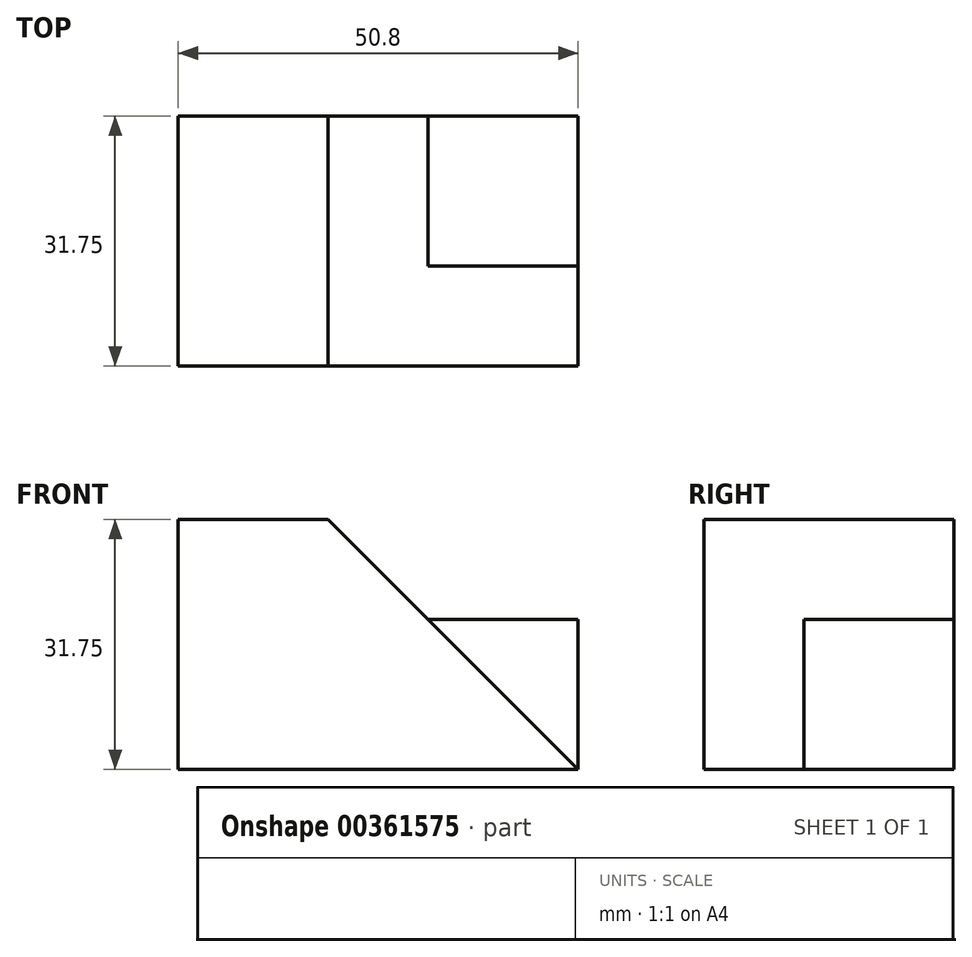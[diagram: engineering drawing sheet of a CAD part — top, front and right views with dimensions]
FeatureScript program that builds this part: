
annotation { "Feature Type Name" : "Feature", "Feature Type Description" : "" }
export const myFeature = defineFeature(function(context is Context, id is Id, definition is map)
    precondition{}
    {
        {
            var Q0;
            Q0=qCreatedBy(makeId("Front.planeOp"),FACE);
            var sketch = newSketch(context, id + "F0", { "sketchPlane" : qUnion([Q0])});
            skLineSegment(sketch, "E0", {"start": v(0, 0) * mm, "end": v(50.8, 0) * mm});
            skLineSegment(sketch, "E1", {"start": v(50.8, 0) * mm, "end": v(50.8, 31.75) * mm});
            skLineSegment(sketch, "E2", {"start": v(50.8, 31.75) * mm, "end": v(0, 31.75) * mm});
            skLineSegment(sketch, "E3", {"start": v(0, 31.75) * mm, "end": v(0, 0) * mm});
            skSolve(sketch);
        }
        {
            var Q0;
            Q0=makeQuery(id+"F0.imprint","IMPRINT",FACE,{"disambiguationData":[TD([[makeQuery(id+"F0.imprint","IMPRINT",EDGE,{"derivedFrom":sQuery(id+"F0.wireOp",EDGE,"E0")}),1.0]])]});
            extrude(context, id + "F1", {"entities" : qUnion([Q0]), "depth" : 31.75 * mm});
        }
        {
            var Q0;
            Q0=makeQuery(id+"F1.opExtrude","CAP_FACE",FACE,{"disambiguationData":[OSD([sQuery(id+"F0.wireOp",EDGE,"E0"),sQuery(id+"F0.wireOp",EDGE,"E1"),sQuery(id+"F0.wireOp",EDGE,"E2"),sQuery(id+"F0.wireOp",EDGE,"E3")])],"isStart":false});
            var sketch = newSketch(context, id + "F2", { "sketchPlane" : qUnion([Q0])});
            skLineSegment(sketch, "E4", {"start": v(19.05, 31.75) * mm, "end": v(31.75, 19.05) * mm});
            skLineSegment(sketch, "E5", {"start": v(31.75, 19.05) * mm, "end": v(50.8, 19.05) * mm});
            skSolve(sketch);
        }
        {
            var Q0;
            {var subQ0=sQuery(id+"F2.wireOp",EDGE,"E4");Q0=makeQuery(id+"F2.imprint","IMPRINT",FACE,{"disambiguationData":[TD([[makeQuery(id+"F2.imprint","IMPRINT",EDGE,{"derivedFrom":subQ0}),1.0]])]});}
            extrude(context, id + "F3", {"entities" : qUnion([Q0]), "operationType" : NewBodyOperationType.REMOVE, "oppositeDirection" : true, "depth" : 31.75 * mm});
        }
        {
            var Q0;
            Q0=makeQuery(id+"F1.opExtrude","CAP_FACE",FACE,{"disambiguationData":[OSD([sQuery(id+"F0.wireOp",EDGE,"E0"),sQuery(id+"F0.wireOp",EDGE,"E1"),sQuery(id+"F0.wireOp",EDGE,"E2"),sQuery(id+"F0.wireOp",EDGE,"E3")])],"isStart":false});
            var sketch = newSketch(context, id + "F4", { "sketchPlane" : qUnion([Q0])});
            skLineSegment(sketch, "E6", {"start": v(31.75, 19.05) * mm, "end": v(50.8, 0) * mm});
            skSolve(sketch);
        }
        {
            var Q0;
            Q0=makeQuery(id+"F4.imprint","IMPRINT",FACE,{"disambiguationData":[TD([[makeQuery(id+"F4.imprint","IMPRINT",EDGE,{"derivedFrom":sQuery(id+"F4.wireOp",EDGE,"E6")}),1.0]])]});
            extrude(context, id + "F5", {"entities" : qUnion([Q0]), "operationType" : NewBodyOperationType.REMOVE, "oppositeDirection" : true, "depth" : 12.7 * mm});
        }
    });
